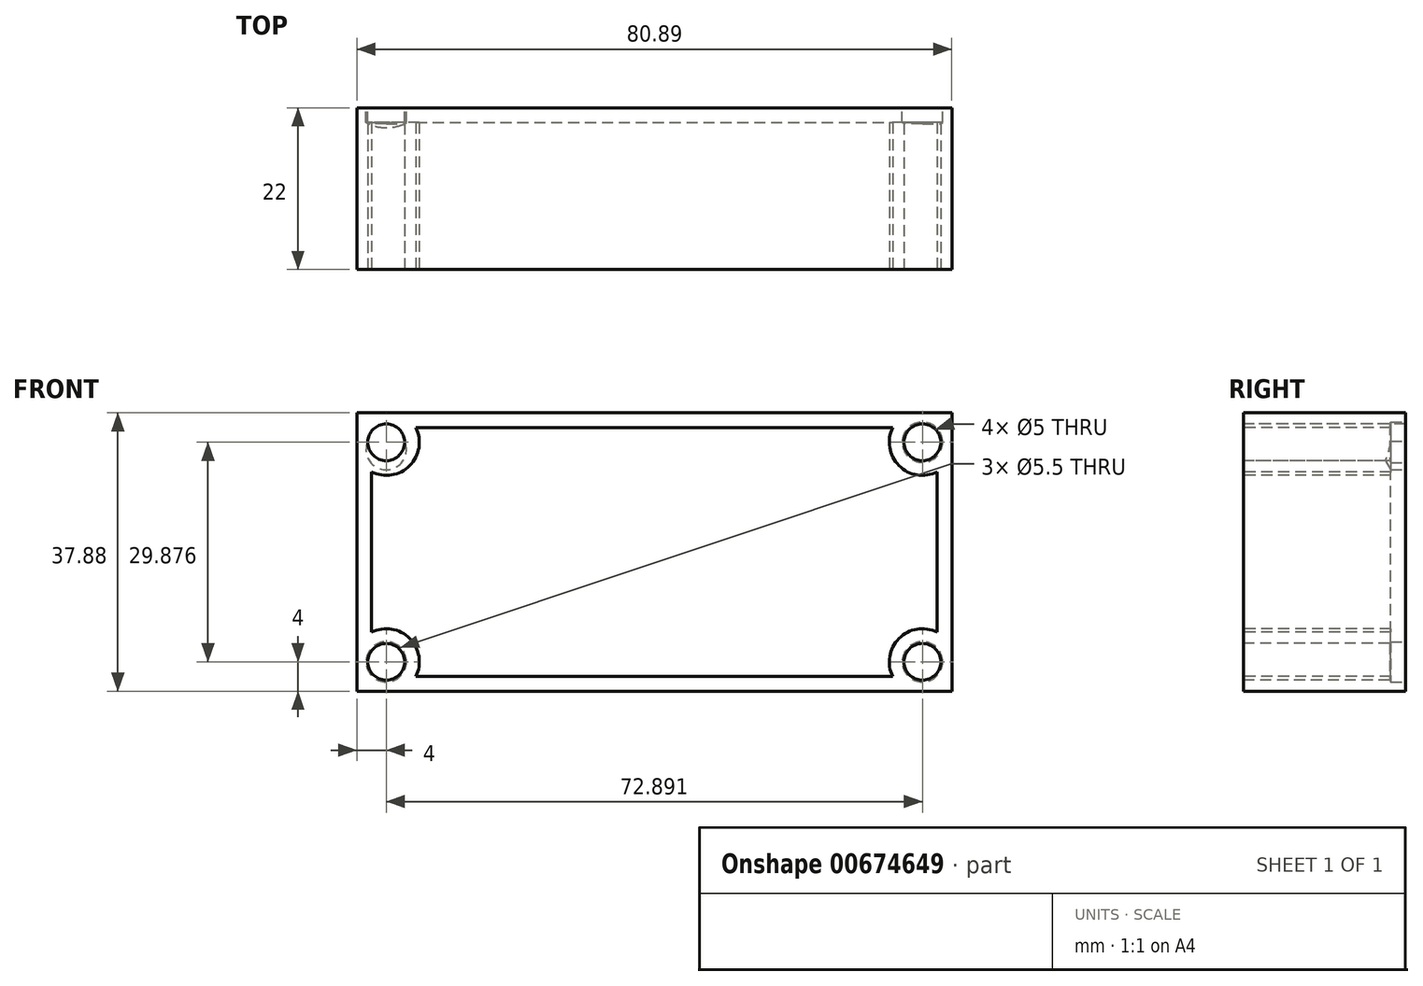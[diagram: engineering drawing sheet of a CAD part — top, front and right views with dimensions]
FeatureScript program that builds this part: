
annotation { "Feature Type Name" : "Feature", "Feature Type Description" : "" }
export const myFeature = defineFeature(function(context is Context, id is Id, definition is map)
    precondition{}
    {
        {
            var Q0;
            Q0=qCreatedBy(makeId("Front.planeOp"),FACE);
            var sketch = newSketch(context, id + "F0", { "sketchPlane" : qUnion([Q0])});
            skLineSegment(sketch, "E0.bottom", {"start": v(0, 0) * mm, "end": v(80.9, 0) * mm});
            skLineSegment(sketch, "E0.top", {"start": v(0, 37.88) * mm, "end": v(80.9, 37.88) * mm});
            skLineSegment(sketch, "E0.left", {"start": v(0, 0) * mm, "end": v(0, 37.88) * mm});
            skLineSegment(sketch, "E0.right", {"start": v(80.9, 0) * mm, "end": v(80.9, 37.88) * mm});
            skSolve(sketch);
        }
        {
            var Q0;
            Q0 = qSketchRegion(id + "F0", true);
            extrude(context, id + "F1", {"entities" : qUnion([Q0]), "depth" : 22 * mm, "offsetDistance" : 25.4 * mm});
        }
        {
            var Q0;
            Q0=makeQuery(id+"F1.opExtrude","CAP_FACE",FACE,{"disambiguationData":[OSD([sQuery(id+"F0.wireOp",EDGE,"E0.bottom"),sQuery(id+"F0.wireOp",EDGE,"E0.top"),sQuery(id+"F0.wireOp",EDGE,"E0.left"),sQuery(id+"F0.wireOp",EDGE,"E0.right")])],"isStart":false});
            var sketch = newSketch(context, id + "F2", { "sketchPlane" : qUnion([Q0])});
            skCircle(sketch, "E1", {"center": v(4, 33.88) * mm, "radius": 1.75 * mm});
            skCircle(sketch, "E2", {"center": v(76.9, 33.88) * mm, "radius": 1.75 * mm});
            skCircle(sketch, "E3", {"center": v(76.9, 4) * mm, "radius": 1.75 * mm});
            skCircle(sketch, "E4", {"center": v(4, 4) * mm, "radius": 1.75 * mm});
            skSolve(sketch);
        }
        {
            var Q0;
            Q0=sQuery(id+"F2.wireOp",VERTEX,"E1.center");
            var Q1;
            Q1=sQuery(id+"F2.wireOp",VERTEX,"E4.center");
            var Q2;
            Q2=sQuery(id+"F2.wireOp",VERTEX,"E3.center");
            var Q3;
            Q3=sQuery(id+"F2.wireOp",VERTEX,"E2.center");
            var Q4;
            Q4=makeQuery(id+"F1.opExtrude","SWEPT_BODY",BODY,{"disambiguationData":[OSD([sQuery(id+"F0.wireOp",EDGE,"E0.bottom"),sQuery(id+"F0.wireOp",EDGE,"E0.top"),sQuery(id+"F0.wireOp",EDGE,"E0.left"),sQuery(id+"F0.wireOp",EDGE,"E0.right")])]});
            hole(context, id + "F3", {"style" : HoleStyle.SIMPLE, "endStyle" : HoleEndStyle.BLIND, "holeDiameter" : 5 * mm, "majorDiameter" : 6.35 * mm, "holeDepth" : 28 * mm, "isTappedThrough" : true, "tappedDepth" : 12.7 * mm, "tapClearance" : 3, "startFromSketch" : true, "locations" : qUnion([Q0, Q1, Q2, Q3]), "scope" : qUnion([Q4])});
        }
        {
            var Q0;
            Q0=makeQuery(id+"F1.opExtrude","CAP_FACE",FACE,{"disambiguationData":[OSD([sQuery(id+"F0.wireOp",EDGE,"E0.bottom"),sQuery(id+"F0.wireOp",EDGE,"E0.top"),sQuery(id+"F0.wireOp",EDGE,"E0.left"),sQuery(id+"F0.wireOp",EDGE,"E0.right")])],"isStart":false});
            shell(context, id + "F4", {"entities" : qUnion([Q0]), "thickness" : 2 * mm});
        }
        {
            var Q0;
            Q0=makeQuery(id+"F1.opExtrude","CAP_FACE",FACE,{"disambiguationData":[OSD([sQuery(id+"F0.wireOp",EDGE,"E0.bottom"),sQuery(id+"F0.wireOp",EDGE,"E0.top"),sQuery(id+"F0.wireOp",EDGE,"E0.left"),sQuery(id+"F0.wireOp",EDGE,"E0.right")])],"isStart":true});
            var sketch = newSketch(context, id + "F5", { "sketchPlane" : qUnion([Q0])});
            skCircle(sketch, "E5.cCircle", {"center": v(-163.22, 16.69) * mm, "radius": 8.75 * mm, "construction": true});
            skLineSegment(sketch, "E5.0", {"start": v(-158.03, 9.64) * mm, "end": v(-166.73, 8.67) * mm});
            skLineSegment(sketch, "E5.1", {"start": v(-166.73, 8.67) * mm, "end": v(-171.92, 15.71) * mm});
            skLineSegment(sketch, "E5.2", {"start": v(-171.92, 15.71) * mm, "end": v(-168.41, 23.73) * mm});
            skLineSegment(sketch, "E5.3", {"start": v(-168.41, 23.73) * mm, "end": v(-159.71, 24.7) * mm});
            skLineSegment(sketch, "E5.4", {"start": v(-159.71, 24.7) * mm, "end": v(-154.52, 17.66) * mm});
            skLineSegment(sketch, "E5.5", {"start": v(-154.52, 17.66) * mm, "end": v(-158.03, 9.64) * mm});
            skCircle(sketch, "E6.cCircle", {"center": v(-167.3, -12.24) * mm, "radius": 8.21 * mm, "construction": true});
            skLineSegment(sketch, "E6.0", {"start": v(-159.5, -17.62) * mm, "end": v(-168.06, -21.69) * mm});
            skLineSegment(sketch, "E6.1", {"start": v(-168.06, -21.69) * mm, "end": v(-175.86, -16.3) * mm});
            skLineSegment(sketch, "E6.2", {"start": v(-175.86, -16.3) * mm, "end": v(-175.1, -6.86) * mm});
            skLineSegment(sketch, "E6.3", {"start": v(-175.1, -6.86) * mm, "end": v(-166.54, -2.79) * mm});
            skLineSegment(sketch, "E6.4", {"start": v(-166.54, -2.79) * mm, "end": v(-158.73, -8.17) * mm});
            skLineSegment(sketch, "E6.5", {"start": v(-158.73, -8.17) * mm, "end": v(-159.5, -17.62) * mm});
            skPoint(sketch, "E6.0.midPoint", {"position": v(-163.78, -19.65) * mm});
            skCircle(sketch, "E7.cCircle", {"center": v(-76.9, 33.88) * mm, "radius": 2.75 * mm, "construction": true});
            skLineSegment(sketch, "E7.0", {"start": v(-73.98, 32.6) * mm, "end": v(-76.54, 30.72) * mm});
            skLineSegment(sketch, "E7.1", {"start": v(-76.54, 30.72) * mm, "end": v(-79.45, 32) * mm});
            skLineSegment(sketch, "E7.2", {"start": v(-79.45, 32) * mm, "end": v(-79.8, 35.15) * mm});
            skLineSegment(sketch, "E7.3", {"start": v(-79.8, 35.15) * mm, "end": v(-77.24, 37.03) * mm});
            skLineSegment(sketch, "E7.4", {"start": v(-77.24, 37.03) * mm, "end": v(-74.33, 35.76) * mm});
            skLineSegment(sketch, "E7.5", {"start": v(-74.33, 35.76) * mm, "end": v(-73.98, 32.6) * mm});
            skPoint(sketch, "E7.0.midPoint", {"position": v(-75.26, 31.66) * mm});
            skCircle(sketch, "E8.cCircle", {"center": v(-76.9, 4) * mm, "radius": 2.75 * mm, "construction": true});
            skLineSegment(sketch, "E8.0", {"start": v(-74.5, 6.1) * mm, "end": v(-73.88, 2.98) * mm});
            skLineSegment(sketch, "E8.1", {"start": v(-73.88, 2.98) * mm, "end": v(-76.27, 0.89) * mm});
            skLineSegment(sketch, "E8.2", {"start": v(-76.27, 0.89) * mm, "end": v(-79.28, 1.9) * mm});
            skLineSegment(sketch, "E8.3", {"start": v(-79.28, 1.9) * mm, "end": v(-79.9, 5.02) * mm});
            skLineSegment(sketch, "E8.4", {"start": v(-79.9, 5.02) * mm, "end": v(-77.51, 7.11) * mm});
            skLineSegment(sketch, "E8.5", {"start": v(-77.51, 7.11) * mm, "end": v(-74.5, 6.1) * mm});
            skPoint(sketch, "E8.0.midPoint", {"position": v(-74.2, 4.54) * mm});
            skCircle(sketch, "E9.cCircle", {"center": v(-4, 32.88) * mm, "radius": 2.75 * mm, "construction": true});
            skLineSegment(sketch, "E9.0", {"start": v(-7, 31.83) * mm, "end": v(-6.4, 34.95) * mm});
            skLineSegment(sketch, "E9.1", {"start": v(-6.4, 34.95) * mm, "end": v(-3.4, 36) * mm});
            skLineSegment(sketch, "E9.2", {"start": v(-3.4, 36) * mm, "end": v(-1, 33.92) * mm});
            skLineSegment(sketch, "E9.3", {"start": v(-1, 33.92) * mm, "end": v(-1.6, 30.8) * mm});
            skLineSegment(sketch, "E9.4", {"start": v(-1.6, 30.8) * mm, "end": v(-4.6, 29.76) * mm});
            skLineSegment(sketch, "E9.5", {"start": v(-4.6, 29.76) * mm, "end": v(-7, 31.83) * mm});
            skPoint(sketch, "E9.0.midPoint", {"position": v(-6.7, 33.4) * mm});
            skCircle(sketch, "E10.cCircle", {"center": v(-4, 4) * mm, "radius": 2.75 * mm, "construction": true});
            skLineSegment(sketch, "E10.0", {"start": v(-1.08, 2.75) * mm, "end": v(-3.62, 0.85) * mm});
            skLineSegment(sketch, "E10.1", {"start": v(-3.62, 0.85) * mm, "end": v(-6.54, 2.1) * mm});
            skLineSegment(sketch, "E10.2", {"start": v(-6.54, 2.1) * mm, "end": v(-6.92, 5.25) * mm});
            skLineSegment(sketch, "E10.3", {"start": v(-6.92, 5.25) * mm, "end": v(-4.38, 7.15) * mm});
            skLineSegment(sketch, "E10.4", {"start": v(-4.38, 7.15) * mm, "end": v(-1.46, 5.9) * mm});
            skLineSegment(sketch, "E10.5", {"start": v(-1.46, 5.9) * mm, "end": v(-1.08, 2.75) * mm});
            skPoint(sketch, "E10.0.midPoint", {"position": v(-2.35, 1.8) * mm});
            skSolve(sketch);
        }
        {
            var Q0;
            Q0=sQuery(id+"F5.wireOp",VERTEX,"E7.cCircle.center");
            var Q1;
            Q1=sQuery(id+"F5.wireOp",VERTEX,"E8.cCircle.center");
            var Q2;
            Q2=sQuery(id+"F5.wireOp",VERTEX,"E10.cCircle.center");
            var Q3;
            Q3=sQuery(id+"F5.wireOp",VERTEX,"E9.cCircle.center");
            var Q4;
            Q4=makeQuery(id+"F1.opExtrude","SWEPT_BODY",BODY,{"disambiguationData":[OSD([sQuery(id+"F0.wireOp",EDGE,"E0.bottom"),sQuery(id+"F0.wireOp",EDGE,"E0.top"),sQuery(id+"F0.wireOp",EDGE,"E0.left"),sQuery(id+"F0.wireOp",EDGE,"E0.right")])]});
            hole(context, id + "F6", {"style" : HoleStyle.SIMPLE, "endStyle" : HoleEndStyle.BLIND, "standardTappedOrClearance" : lookupTablePath({ "standard" : "ISO", "fit" : "Normal", "size" : "M5", "type" : "Clearance" }), "standardBlindInLast" : lookupTablePath({ "fit" : "Standard", "standard" : "ISO", "size" : "M5", "type" : "Clearance" }), "holeDiameter" : 5.5 * mm, "majorDiameter" : 6.35 * mm, "holeDepth" : 2 * mm, "isTappedThrough" : true, "tappedDepth" : 12.7 * mm, "tapClearance" : 3, "startFromSketch" : true, "locations" : qUnion([Q0, Q1, Q2, Q3]), "scope" : qUnion([Q4])});
        }
    });
